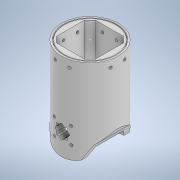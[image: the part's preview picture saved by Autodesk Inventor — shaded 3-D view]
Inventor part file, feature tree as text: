
AUTODESK INVENTOR PART (.ipt)
format: ipt  version: 2021 (Build 250183000, 183)  size: 288,768 bytes
history: native  units: mm
features: sketch x9, extrude x8
ambient origin geometry x8: Origin, YZ Plane, XZ Plane, XY Plane, X Axis, Y Axis, Z Axis, Center Point
bodies: Body1 (feature_tree)
feature tree (17):
  extrude  "Extrusión2"  Depth=100.0mm TaperAngle=0.0deg
  sketch  "Boceto5"  dims[d45=100.0mm d46=0.0mm d53=10.0mm]
  sketch  "Boceto6"  dims[d54=10.0mm d55=25.0mm]
  sketch  "Boceto7"  dims[d58=20.0mm d59=20.0mm]
  extrude  "Extrusión4"  Depth=10.0mm
  extrude  "Extrusión8"  Depth=10.0mm
  extrude  "Extrusión10"  Depth=20.0mm
  extrude  "Extrusión12"  Depth=30.0mm
  extrude  "Extrusión13"  Depth=200.0mm TaperAngle=0.0deg
  extrude  "Extrusión14"  Depth=8.0mm
  extrude  "Extrusión15"  Depth=8.0mm
  sketch  "Boceto14"  dims[d99=8.0mm d100=3.0mm d101=200.0mm d102=0.0mm d111=200.0mm d112=0.0mm d113=59.0mm d114=61.0mm d115=2.5mm d116=0.0mm d119=40.0mm d121=360.0deg d123=200.0mm d124=0.0mm d11=0.5mm d12=0.872665mm d13=0.5mm d14=0.872665mm d30=0.5mm d31=0.872665mm d36=0.5mm d37=0.872665mm d38=0.5mm d39=0.872665mm d47=0.5mm d48=0.872665mm d49=0.5mm d50=0.872665mm d68=0.5mm d69=0.872665mm d70=0.5mm d71=0.872665mm]
  sketch  "Boceto4"  dims[d20=40.0mm d22=360.0deg d28=100.0mm d29=0.0mm]
  sketch  "Boceto10"  dims[d60=30.0mm d61=30.0mm]
  sketch  "Boceto11"  dims[d62=200.0mm d63=0.0mm d77=200.0mm d78=0.0mm]
  sketch  "Boceto12"  dims[d95=8.0mm d96=8.0mm]
  sketch  "Boceto13"  dims[d97=3.0mm d98=8.0mm]
